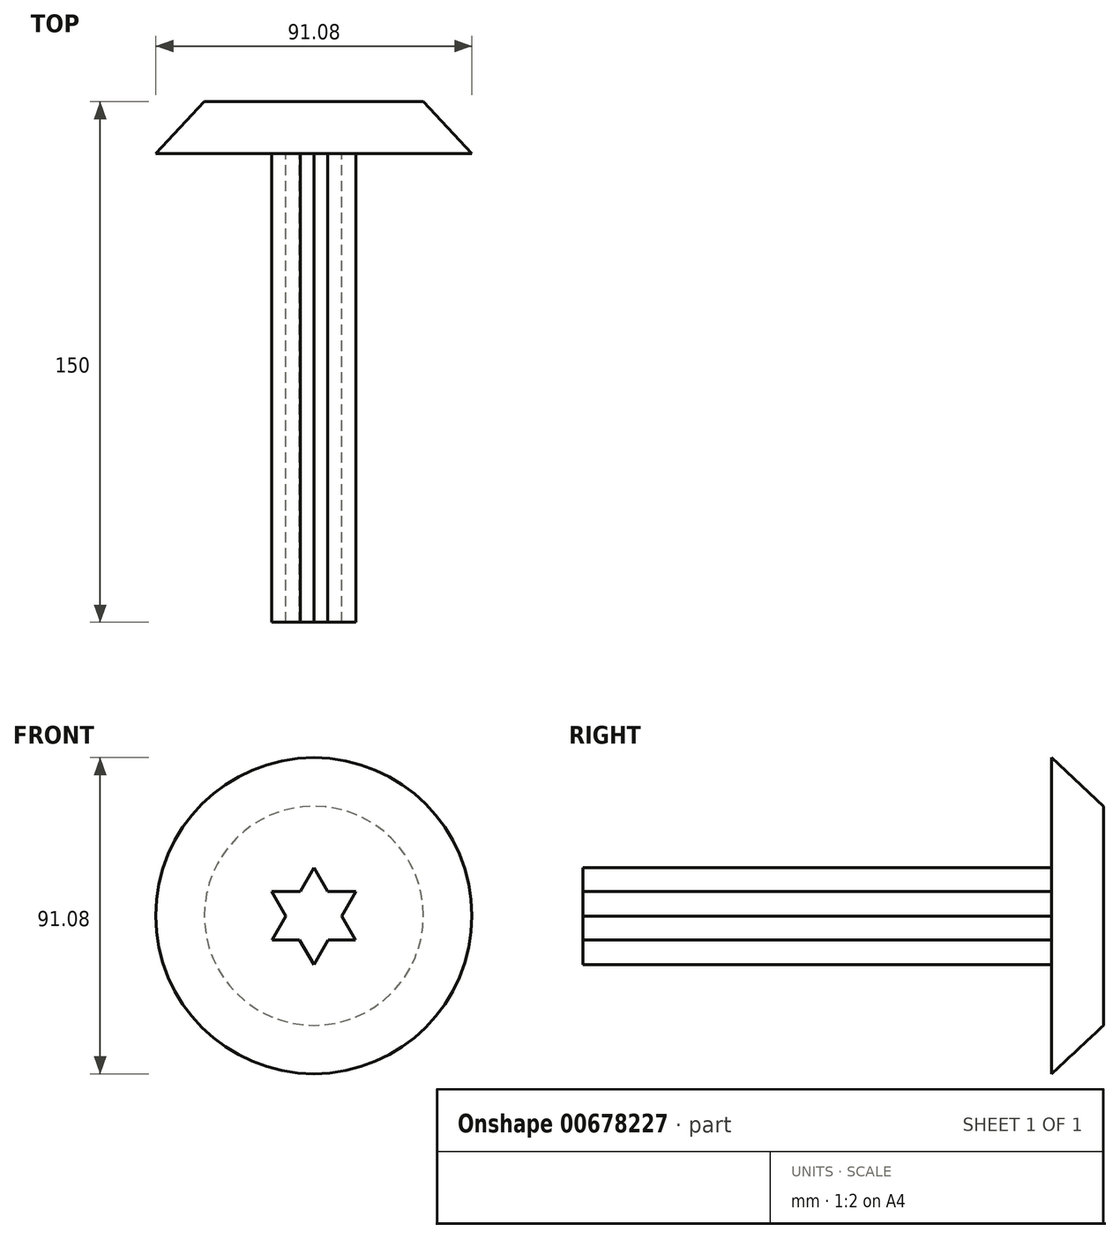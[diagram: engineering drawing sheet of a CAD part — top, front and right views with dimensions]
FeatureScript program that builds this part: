
annotation { "Feature Type Name" : "Feature", "Feature Type Description" : "" }
export const myFeature = defineFeature(function(context is Context, id is Id, definition is map)
    precondition{}
    {
        {
            var Q0;
            Q0=qCreatedBy(makeId("Front.planeOp"),FACE);
            var sketch = newSketch(context, id + "F0", { "sketchPlane" : qUnion([Q0])});
            skLineSegment(sketch, "E0.0", {"start": v(12, -6.93) * mm, "end": v(4.11, -6.93) * mm});
            skLineSegment(sketch, "E0.1", {"start": v(-12, -6.93) * mm, "end": v(-8.06, -0.1) * mm});
            skLineSegment(sketch, "E0.2", {"start": v(0, 13.86) * mm, "end": v(3.94, 7.03) * mm});
            skLineSegment(sketch, "E1.0", {"start": v(-12.17, 7.03) * mm, "end": v(-3.94, 7.03) * mm});
            skLineSegment(sketch, "E1.1", {"start": v(12.17, 7.03) * mm, "end": v(8.06, -0.1) * mm});
            skLineSegment(sketch, "E1.2", {"start": v(0, -14.05) * mm, "end": v(-4.11, -6.93) * mm});
            skLineSegment(sketch, "E2.trimOffspring", {"start": v(3.94, 7.03) * mm, "end": v(12.17, 7.03) * mm});
            skLineSegment(sketch, "E3.trimOffspring", {"start": v(-3.94, 7.03) * mm, "end": v(0, 13.86) * mm});
            skLineSegment(sketch, "E4.trimOffspring", {"start": v(-8.06, -0.1) * mm, "end": v(-12.17, 7.03) * mm});
            skLineSegment(sketch, "E5.trimOffspring", {"start": v(-4.11, -6.93) * mm, "end": v(-12, -6.93) * mm});
            skLineSegment(sketch, "E6.trimOffspring", {"start": v(8.06, -0.1) * mm, "end": v(12, -6.93) * mm});
            skLineSegment(sketch, "E7.trimOffspring", {"start": v(4.11, -6.93) * mm, "end": v(0, -14.05) * mm});
            skSolve(sketch);
        }
        {
            var Q0;
            Q0=makeQuery(id+"F0.imprint","IMPRINT",FACE,{"disambiguationData":[TD([[makeQuery(id+"F0.imprint","IMPRINT",EDGE,{"derivedFrom":sQuery(id+"F0.wireOp",EDGE,"E0.0")}),-1.0]])]});
            var Q1;
            Q1=sQuery(id+"F0.wireOp",EDGE,"E0.0");
            var Q2;
            Q2=sQuery(id+"F0.wireOp",EDGE,"E0.1");
            var Q3;
            Q3=sQuery(id+"F0.wireOp",EDGE,"E0.2");
            var Q4;
            Q4=sQuery(id+"F0.wireOp",EDGE,"E1.0");
            var Q5;
            Q5=sQuery(id+"F0.wireOp",EDGE,"E1.1");
            var Q6;
            Q6=sQuery(id+"F0.wireOp",EDGE,"E1.2");
            extrude(context, id + "F1", {"entities" : qUnion([Q0]), "surfaceEntities" : qUnion([Q1, Q2, Q3, Q4, Q5, Q6]), "depth" : 150 * mm, "offsetDistance" : 25 * mm});
        }
        {
            var Q0;
            Q0=qCreatedBy(makeId("Front.planeOp"),FACE);
            var sketch = newSketch(context, id + "F2", { "sketchPlane" : qUnion([Q0])});
            skCircle(sketch, "E8", {"center": v(0, 0) * mm, "radius": 31.56 * mm});
            skSolve(sketch);
        }
        {
            var Q0;
            Q0 = qSketchRegion(id + "F2", true);
            extrude(context, id + "F3", {"entities" : qUnion([Q0]), "operationType" : NewBodyOperationType.ADD, "depth" : 15 * mm, "offsetDistance" : 25 * mm, "hasDraft" : true, "draftAngle" : 43 * degree});
        }
    });
